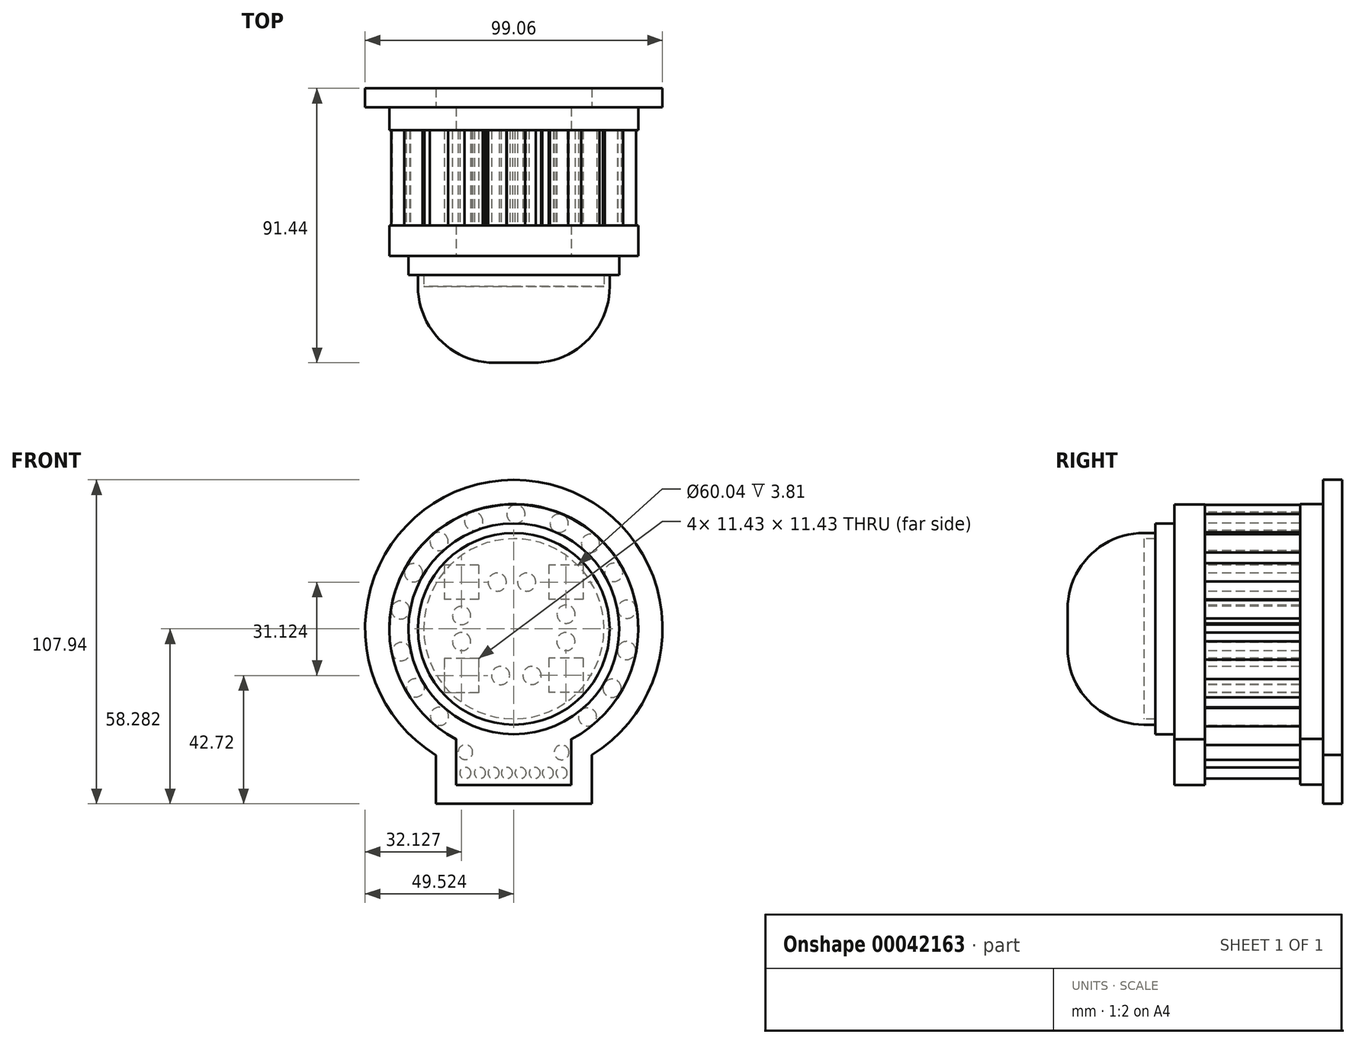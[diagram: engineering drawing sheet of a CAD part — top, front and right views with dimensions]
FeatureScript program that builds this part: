
annotation { "Feature Type Name" : "Feature", "Feature Type Description" : "" }
export const myFeature = defineFeature(function(context is Context, id is Id, definition is map)
    precondition{}
    {
        {
            var Q0;
            Q0=qCreatedBy(makeId("Front.planeOp"),FACE);
            var sketch = newSketch(context, id + "F0", { "sketchPlane" : qUnion([Q0])});
            skCircle(sketch, "E0", {"center": v(-51.32, 52.9) * mm, "radius": 31.92 * mm});
            skLineSegment(sketch, "E1", {"start": v(-51.32, 20.98) * mm, "end": v(38.62, 20.98) * mm});
            skLineSegment(sketch, "E2", {"start": v(38.62, 20.98) * mm, "end": v(-125, 20.98) * mm});
            skSolve(sketch);
        }
        {
            var Q0;
            Q0=makeQuery(id+"F0.imprint","IMPRINT",FACE,{"disambiguationData":[TD([[makeQuery(id+"F0.imprint","IMPRINT",EDGE,{"derivedFrom":sQuery(id+"F0.wireOp",EDGE,"E0")}),1.0]])]});
            extrude(context, id + "F1", {"entities" : qUnion([Q0]), "depth" : 25.4 * mm});
        }
        {
            var Q0;
            Q0=makeQuery(id+"F1.opExtrude","CAP_FACE",FACE,{"disambiguationData":[OSD([sQuery(id+"F0.wireOp",EDGE,"E0")])],"isStart":false});
            fillet(context, id + "F2", {"entities" : qUnion([Q0]), "radius" : 25.4 * mm, "tangentPropagation" : true, "allowEdgeOverflow" : false});
        }
        {
            var Q0;
            Q0=makeQuery(id+"F1.opExtrude","CAP_FACE",FACE,{"disambiguationData":[OSD([sQuery(id+"F0.wireOp",EDGE,"E0")])],"isStart":true});
            var sketch = newSketch(context, id + "F3", { "sketchPlane" : qUnion([Q0])});
            skCircle(sketch, "E3.0", {"center": v(51.32, 52.9) * mm, "radius": 30.02 * mm});
            skSolve(sketch);
        }
        {
            var Q0;
            Q0=makeQuery(id+"F3.imprint","IMPRINT",FACE,{"disambiguationData":[TD([[makeQuery(id+"F3.imprint","IMPRINT",EDGE,{"derivedFrom":sQuery(id+"F3.wireOp",EDGE,"E3.0")}),-1.0]])]});
            extrude(context, id + "F4", {"entities" : qUnion([Q0]), "operationType" : NewBodyOperationType.ADD, "depth" : 3.8 * mm});
        }
        {
            var Q0;
            Q0=makeQuery(id+"F4.opExtrude","CAP_FACE",FACE,{"disambiguationData":[OSD([sQuery(id+"F3.wireOp",EDGE,"E3.0")])],"isStart":false});
            var sketch = newSketch(context, id + "F5", { "sketchPlane" : qUnion([Q0])});
            skCircle(sketch, "E4.0", {"center": v(51.32, 52.9) * mm, "radius": 35.1 * mm});
            skSolve(sketch);
        }
        {
            var Q0;
            Q0 = qSketchRegion(id + "F5", true);
            extrude(context, id + "F6", {"entities" : qUnion([Q0]), "operationType" : NewBodyOperationType.ADD, "depth" : 6.35 * mm});
        }
        {
            var Q0;
            Q0=makeQuery(id+"F6.opExtrude","CAP_FACE",FACE,{"disambiguationData":[OSD([sQuery(id+"F5.wireOp",EDGE,"E4.0")])],"isStart":false});
            var sketch = newSketch(context, id + "F7", { "sketchPlane" : qUnion([Q0])});
            skArc(sketch, "E5.0", {"start": v(70.5, 16.16) * mm, "mid": v(51.32, 94.35) * mm, "end": v(32.12, 16.16) * mm});
            skLineSegment(sketch, "E6", {"start": v(70.5, 16.16) * mm, "end": v(32.12, 16.16) * mm});
            skSolve(sketch);
        }
        {
            var Q0;
            Q0=makeQuery(id+"F7.imprint","IMPRINT",FACE,{"disambiguationData":[TD([[makeQuery(id+"F7.imprint","IMPRINT",EDGE,{"derivedFrom":sQuery(id+"F7.wireOp",EDGE,"E5.0")}),1.0]])]});
            extrude(context, id + "F8", {"entities" : qUnion([Q0]), "depth" : 10.16 * mm});
        }
        {
            var Q0;
            Q0=makeQuery(id+"F7.imprint","IMPRINT",FACE,{"disambiguationData":[TD([[makeQuery(id+"F7.imprint","IMPRINT",EDGE,{"derivedFrom":makeQuery(id+"F6.opExtrude","CAP_EDGE",EDGE,{"disambiguationData":[OSD([sQuery(id+"F5.wireOp",EDGE,"E4.0")])],"isStart":false})}),1.0]])]});
            extrude(context, id + "F9", {"entities" : qUnion([Q0]), "operationType" : NewBodyOperationType.ADD, "depth" : 10.16 * mm});
        }
        {
            var Q0;
            Q0=makeQuery(id+"F8.opExtrude","SWEPT_FACE",FACE,{"disambiguationData":[OSD([sQuery(id+"F7.wireOp",EDGE,"E6")])]});
            var sketch = newSketch(context, id + "F10", { "sketchPlane" : qUnion([Q0])});
            skLineSegment(sketch, "E7.bottom", {"start": v(-70.5, -10.16) * mm, "end": v(-32.12, -10.16) * mm});
            skLineSegment(sketch, "E7.top", {"start": v(-70.5, -20.32) * mm, "end": v(-32.12, -20.32) * mm});
            skLineSegment(sketch, "E7.left", {"start": v(-70.5, -10.16) * mm, "end": v(-70.5, -20.32) * mm});
            skLineSegment(sketch, "E7.right", {"start": v(-32.12, -10.16) * mm, "end": v(-32.12, -20.32) * mm});
            skSolve(sketch);
        }
        {
            var Q0;
            Q0=makeQuery(id+"F10.imprint","IMPRINT",FACE,{"disambiguationData":[TD([[makeQuery(id+"F10.imprint","IMPRINT",EDGE,{"derivedFrom":sQuery(id+"F10.wireOp",EDGE,"E7.bottom")}),-1.0]])]});
            extrude(context, id + "F11", {"entities" : qUnion([Q0]), "operationType" : NewBodyOperationType.ADD, "depth" : 15.24 * mm});
        }
        {
            var Q0;
            Q0=makeQuery(id+"F11.boolean.opBoolean","MERGE",FACE,{"derivedFrom":[makeQuery(id+"F8.opExtrude","CAP_FACE",FACE,{"disambiguationData":[OSD([sQuery(id+"F5.wireOp",EDGE,"E4.0"),sQuery(id+"F7.wireOp",EDGE,"E5.0"),sQuery(id+"F7.wireOp",EDGE,"E6")])],"isStart":false}),makeQuery(id+"F11.opExtrude","SWEPT_FACE",FACE,{"disambiguationData":[OSD([sQuery(id+"F10.wireOp",EDGE,"E7.top")])]})]});
            var sketch = newSketch(context, id + "F12", { "sketchPlane" : qUnion([Q0])});
            skCircle(sketch, "E8", {"center": v(67.45, 4.89) * mm, "radius": 1.86 * mm});
            skCircle(sketch, "E9", {"center": v(35.4, 4.89) * mm, "radius": 1.86 * mm});
            skCircle(sketch, "E10", {"center": v(39.96, 4.89) * mm, "radius": 1.86 * mm});
            skCircle(sketch, "E11", {"center": v(44.37, 4.89) * mm, "radius": 1.86 * mm});
            skCircle(sketch, "E12", {"center": v(49.07, 4.89) * mm, "radius": 1.86 * mm});
            skCircle(sketch, "E13", {"center": v(53.63, 4.89) * mm, "radius": 1.86 * mm});
            skCircle(sketch, "E14", {"center": v(58.04, 4.89) * mm, "radius": 1.86 * mm});
            skCircle(sketch, "E15", {"center": v(62.6, 4.89) * mm, "radius": 1.86 * mm});
            skCircle(sketch, "E16", {"center": v(35.4, 11.72) * mm, "radius": 2.47 * mm});
            skCircle(sketch, "E17", {"center": v(67.45, 11.8) * mm, "radius": 2.44 * mm});
            skCircle(sketch, "E18", {"center": v(13.6, 59.42) * mm, "radius": 3.04 * mm});
            skCircle(sketch, "E19", {"center": v(50.63, 91.12) * mm, "radius": 3.04 * mm});
            skCircle(sketch, "E20", {"center": v(18.58, 33.1) * mm, "radius": 3.04 * mm});
            skCircle(sketch, "E21", {"center": v(25.8, 81.4) * mm, "radius": 3.04 * mm});
            skCircle(sketch, "E22", {"center": v(89.08, 59.2) * mm, "radius": 3.04 * mm});
            skCircle(sketch, "E23", {"center": v(84.09, 33.24) * mm, "radius": 3.04 * mm});
            skCircle(sketch, "E24", {"center": v(76.2, 81.98) * mm, "radius": 3.04 * mm});
            skCircle(sketch, "E25", {"center": v(36.2, 88.06) * mm, "radius": 3.04 * mm});
            skCircle(sketch, "E26", {"center": v(88.8, 45.32) * mm, "radius": 3.04 * mm});
            skCircle(sketch, "E27", {"center": v(18.02, 71.69) * mm, "radius": 3.04 * mm});
            skCircle(sketch, "E28", {"center": v(13.76, 45.65) * mm, "radius": 3.04 * mm});
            skCircle(sketch, "E29", {"center": v(64.68, 88.75) * mm, "radius": 3.04 * mm});
            skCircle(sketch, "E30", {"center": v(84.72, 71.6) * mm, "radius": 3.04 * mm});
            skCircle(sketch, "E31", {"center": v(26.76, 23.53) * mm, "radius": 3.04 * mm});
            skCircle(sketch, "E32", {"center": v(76.07, 23.76) * mm, "radius": 3.04 * mm});
            skCircle(sketch, "E33", {"center": v(853.83, 233.1) * mm, "radius": 3.04 * mm});
            skLineSegment(sketch, "E34.bottom", {"start": v(63, 74.18) * mm, "end": v(74.43, 74.18) * mm});
            skLineSegment(sketch, "E34.top", {"start": v(63, 62.75) * mm, "end": v(74.43, 62.75) * mm});
            skLineSegment(sketch, "E34.left", {"start": v(63, 74.18) * mm, "end": v(63, 62.75) * mm});
            skLineSegment(sketch, "E34.right", {"start": v(74.43, 74.18) * mm, "end": v(74.43, 62.75) * mm});
            skLineSegment(sketch, "E35.left", {"start": v(28.27, 43.1) * mm, "end": v(28.27, 31.66) * mm});
            skLineSegment(sketch, "E35.right", {"start": v(39.7, 43.1) * mm, "end": v(39.7, 31.66) * mm});
            skLineSegment(sketch, "E35.top", {"start": v(28.27, 31.66) * mm, "end": v(39.7, 31.66) * mm});
            skLineSegment(sketch, "E35.bottom", {"start": v(28.27, 43.1) * mm, "end": v(39.7, 43.1) * mm});
            skLineSegment(sketch, "E36.left", {"start": v(28.2, 74.18) * mm, "end": v(28.2, 62.75) * mm});
            skLineSegment(sketch, "E36.right", {"start": v(39.63, 74.18) * mm, "end": v(39.63, 62.75) * mm});
            skLineSegment(sketch, "E36.top", {"start": v(28.2, 62.75) * mm, "end": v(39.63, 62.75) * mm});
            skLineSegment(sketch, "E36.bottom", {"start": v(28.2, 74.18) * mm, "end": v(39.63, 74.18) * mm});
            skLineSegment(sketch, "E37.left", {"start": v(63, 43.05) * mm, "end": v(63, 31.62) * mm});
            skLineSegment(sketch, "E37.right", {"start": v(74.43, 43.05) * mm, "end": v(74.43, 31.62) * mm});
            skLineSegment(sketch, "E37.top", {"start": v(63, 31.62) * mm, "end": v(74.43, 31.62) * mm});
            skLineSegment(sketch, "E37.bottom", {"start": v(63, 43.05) * mm, "end": v(74.43, 43.05) * mm});
            skLineSegment(sketch, "E38", {"start": v(74.43, 31.62) * mm, "end": v(63, 31.62) * mm});
            skCircle(sketch, "E39", {"center": v(33.98, 48.66) * mm, "radius": 3.04 * mm});
            skCircle(sketch, "E40", {"center": v(33.91, 57.78) * mm, "radius": 3.04 * mm});
            skCircle(sketch, "E41", {"center": v(56.83, 68.46) * mm, "radius": 3.04 * mm});
            skCircle(sketch, "E42", {"center": v(68.71, 57.34) * mm, "radius": 3.04 * mm});
            skCircle(sketch, "E43", {"center": v(68.71, 48.66) * mm, "radius": 3.04 * mm});
            skCircle(sketch, "E44", {"center": v(55.72, 37.34) * mm, "radius": 3.04 * mm});
            skCircle(sketch, "E45", {"center": v(47.04, 68.46) * mm, "radius": 3.04 * mm});
            skCircle(sketch, "E46", {"center": v(45.26, 37.38) * mm, "radius": 3.04 * mm});
            skPoint(sketch, "E47", {"position": v(63, 37.34) * mm});
            skPoint(sketch, "E48", {"position": v(39.7, 37.38) * mm});
            skPoint(sketch, "E49", {"position": v(33.98, 43.1) * mm});
            skPoint(sketch, "E50", {"position": v(33.91, 62.75) * mm});
            skPoint(sketch, "E51", {"position": v(39.63, 68.46) * mm});
            skPoint(sketch, "E52", {"position": v(63, 68.46) * mm});
            skPoint(sketch, "E53", {"position": v(68.71, 43.05) * mm});
            skPoint(sketch, "E54", {"position": v(68.71, 62.75) * mm});
            skSolve(sketch);
        }
        {
            var Q0;
            Q0 = qSketchRegion(id + "F12", true);
            extrude(context, id + "F13", {"entities" : qUnion([Q0]), "operationType" : NewBodyOperationType.ADD, "depth" : 31.75 * mm});
        }
        {
            var Q0;
            Q0=makeQuery(id+"F13.opExtrude","CAP_FACE",FACE,{"disambiguationData":[OSD([sQuery(id+"F12.wireOp",EDGE,"E26")])],"isStart":false});
            var sketch = newSketch(context, id + "F14", { "sketchPlane" : qUnion([Q0])});
            skArc(sketch, "E55.0", {"start": v(70.5, 16.3) * mm, "mid": v(51.31, 94.47) * mm, "end": v(32.12, 16.3) * mm});
            skLineSegment(sketch, "E56.bottom", {"start": v(70.5, 16.3) * mm, "end": v(70.52, 16.3) * mm});
            skLineSegment(sketch, "E56.top", {"start": v(32.12, 1.02) * mm, "end": v(70.52, 1.02) * mm});
            skLineSegment(sketch, "E56.left", {"start": v(32.12, 16.3) * mm, "end": v(32.12, 1.02) * mm});
            skLineSegment(sketch, "E56.right", {"start": v(70.52, 16.3) * mm, "end": v(70.52, 1.02) * mm});
            skSolve(sketch);
        }
        {
            var Q0;
            Q0 = qSketchRegion(id + "F14", true);
            extrude(context, id + "F15", {"entities" : qUnion([Q0]), "operationType" : NewBodyOperationType.ADD, "depth" : 7.62 * mm});
        }
        {
            var Q0;
            Q0=makeQuery(id+"F13.opExtrude","SWEPT_BODY",BODY,{"disambiguationData":[OSD([sQuery(id+"F12.wireOp",EDGE,"E33")])]});
            deleteBodies(context, id + "F16", {"entities" : qUnion([Q0])});
        }
        {
            var Q0;
            Q0=makeQuery(id+"F15.opExtrude","CAP_FACE",FACE,{"disambiguationData":[OSD([sQuery(id+"F14.wireOp",EDGE,"E55.0"),sQuery(id+"F14.wireOp",EDGE,"E56.bottom"),sQuery(id+"F14.wireOp",EDGE,"E56.top"),sQuery(id+"F14.wireOp",EDGE,"E56.left"),sQuery(id+"F14.wireOp",EDGE,"E56.right")])],"isStart":false});
            var sketch = newSketch(context, id + "F17", { "sketchPlane" : qUnion([Q0])});
            skArc(sketch, "E57", {"start": v(77.23, 10.82) * mm, "mid": v(51.33, 102.56) * mm, "end": v(25.38, 10.83) * mm});
            skLineSegment(sketch, "E58.left", {"start": v(32.12, 16.3) * mm, "end": v(32.12, 16.3) * mm});
            skLineSegment(sketch, "E58.right", {"start": v(70.52, 16.3) * mm, "end": v(70.52, 16.3) * mm});
            skLineSegment(sketch, "E59.bottom", {"start": v(32.12, 16.3) * mm, "end": v(70.52, 16.3) * mm});
            skLineSegment(sketch, "E59.top", {"start": v(32.12, 1.02) * mm, "end": v(70.52, 1.02) * mm});
            skLineSegment(sketch, "E60.top", {"start": v(25.38, -5.38) * mm, "end": v(77.23, -5.38) * mm});
            skLineSegment(sketch, "E60.left", {"start": v(25.38, 10.83) * mm, "end": v(25.38, -5.38) * mm});
            skLineSegment(sketch, "E60.right", {"start": v(77.23, 10.83) * mm, "end": v(77.23, -5.38) * mm});
            skSolve(sketch);
        }
        {
            var Q0;
            Q0 = qSketchRegion(id + "F17", true);
            extrude(context, id + "F18", {"entities" : qUnion([Q0]), "operationType" : NewBodyOperationType.ADD, "depth" : 6.35 * mm});
        }
    });
